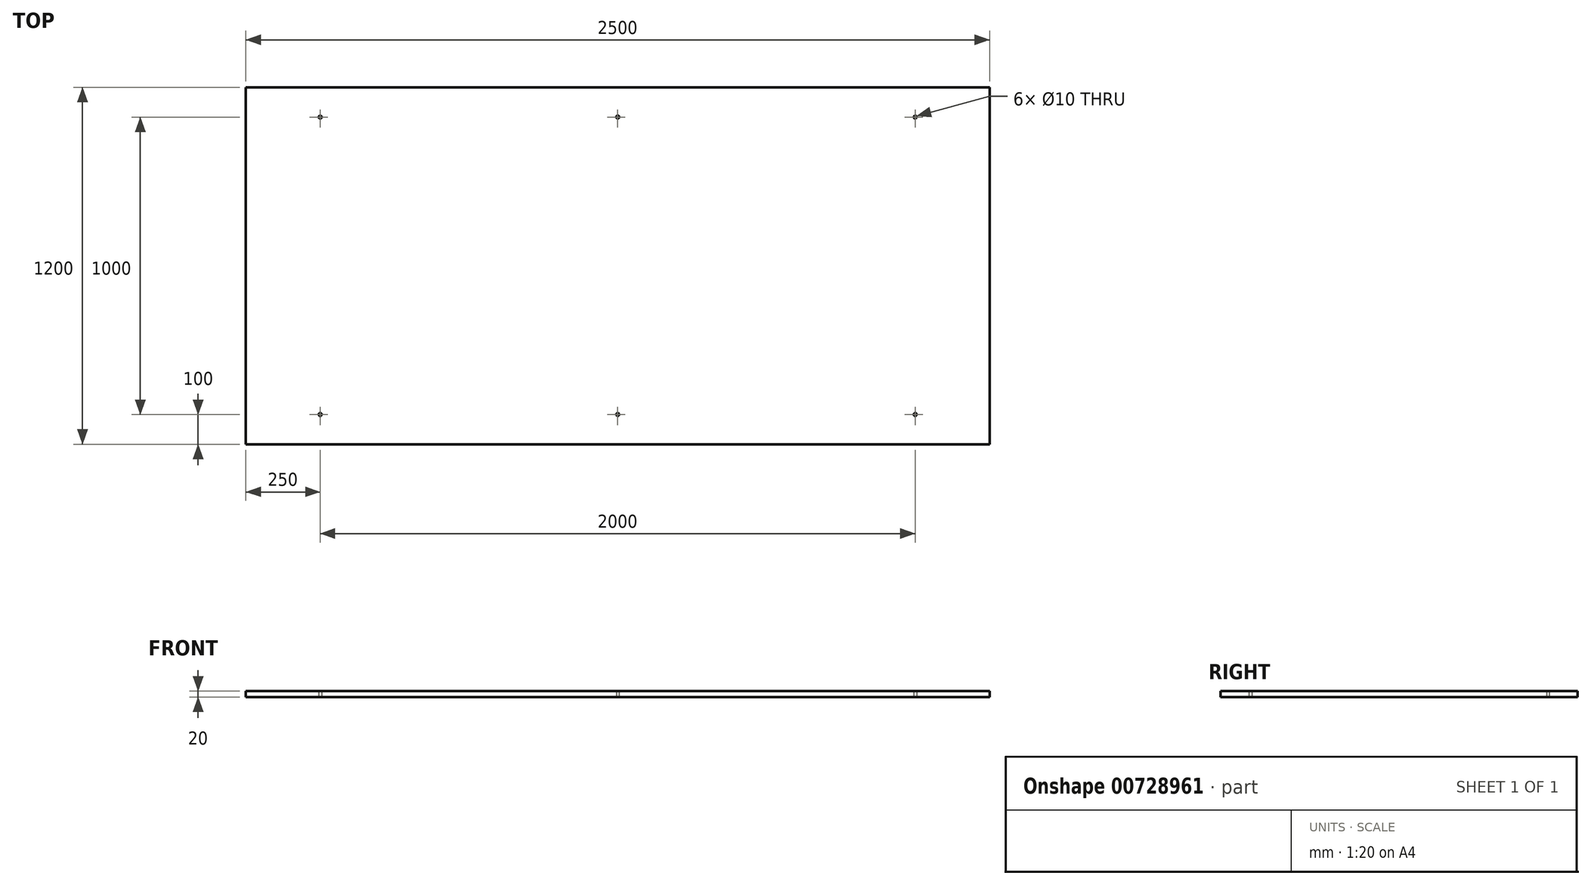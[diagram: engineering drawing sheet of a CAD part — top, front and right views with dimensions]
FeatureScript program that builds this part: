
annotation { "Feature Type Name" : "Feature", "Feature Type Description" : "" }
export const myFeature = defineFeature(function(context is Context, id is Id, definition is map)
    precondition{}
    {
        {
            var Q0;
            Q0=qCreatedBy(makeId("Top.planeOp"),FACE);
            var sketch = newSketch(context, id + "F0", { "sketchPlane" : qUnion([Q0])});
            skLineSegment(sketch, "E0.bottom", {"start": v(1250, 600) * mm, "end": v(-1250, 600) * mm});
            skLineSegment(sketch, "E0.top", {"start": v(1250, -600) * mm, "end": v(-1250, -600) * mm});
            skLineSegment(sketch, "E0.left", {"start": v(1250, 600) * mm, "end": v(1250, -600) * mm});
            skLineSegment(sketch, "E0.right", {"start": v(-1250, 600) * mm, "end": v(-1250, -600) * mm});
            skPoint(sketch, "E0.middle", {"position": v(0, 0) * mm});
            skCircle(sketch, "E1", {"center": v(1000, -500) * mm, "radius": 5 * mm});
            skCircle(sketch, "E2", {"center": v(1000, 500) * mm, "radius": 5 * mm});
            skCircle(sketch, "E3", {"center": v(-1000, -500) * mm, "radius": 5 * mm});
            skCircle(sketch, "E4", {"center": v(-1000, 500) * mm, "radius": 5 * mm});
            skCircle(sketch, "E5", {"center": v(0, -500) * mm, "radius": 5 * mm});
            skCircle(sketch, "E6", {"center": v(0, 500) * mm, "radius": 5 * mm});
            skSolve(sketch);
        }
        {
            var Q0;
            Q0 = qSketchRegion(id + "F0", true);
            extrude(context, id + "F1", {"entities" : qUnion([Q0]), "depth" : 20 * mm, "offsetDistance" : 25 * mm});
        }
    });
